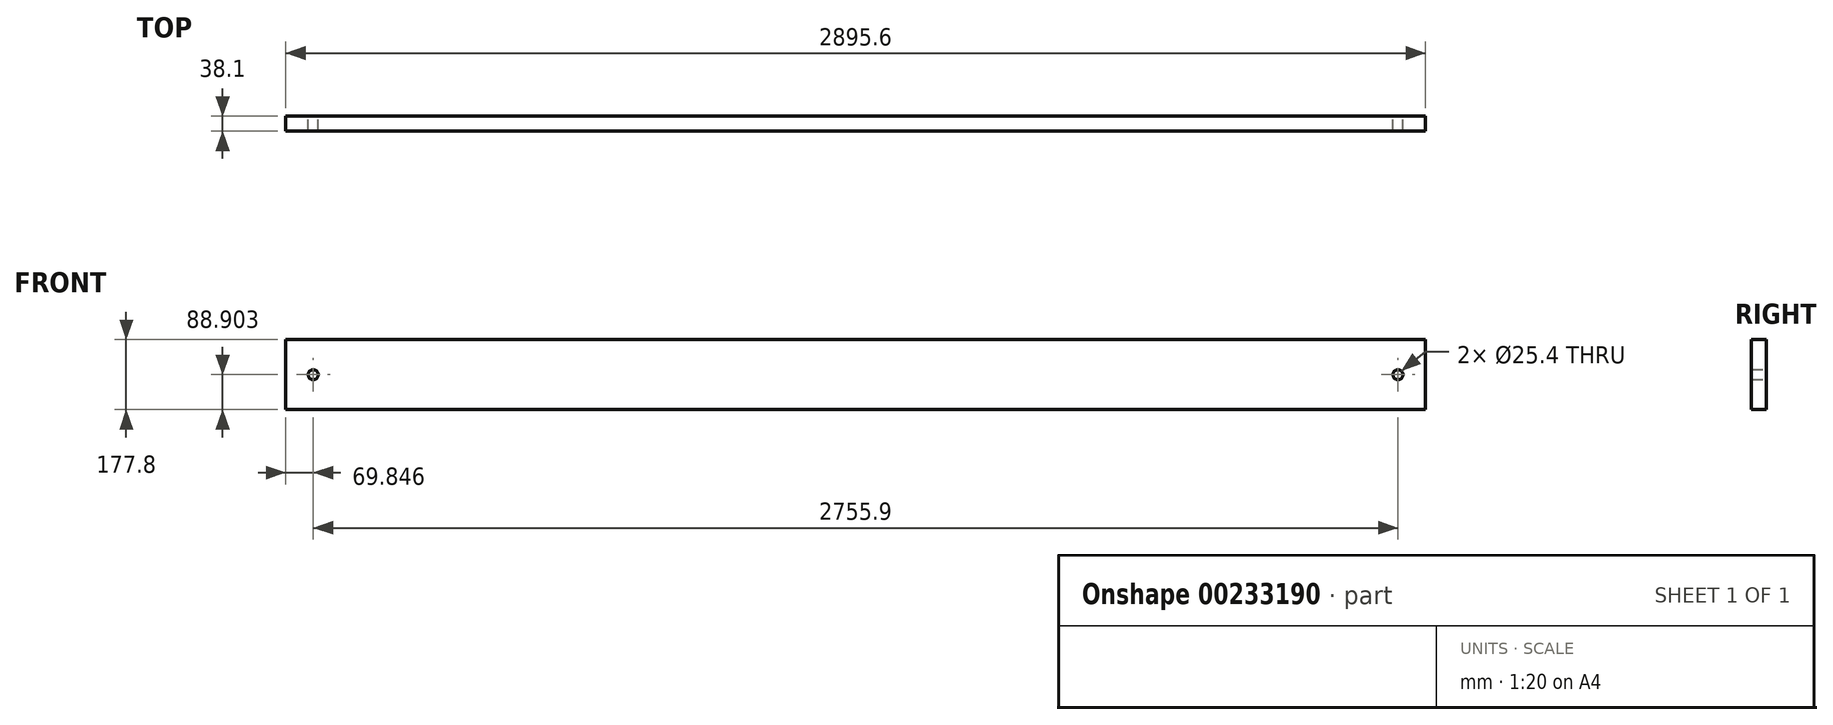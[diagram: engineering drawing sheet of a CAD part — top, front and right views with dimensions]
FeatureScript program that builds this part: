
annotation { "Feature Type Name" : "Feature", "Feature Type Description" : "" }
export const myFeature = defineFeature(function(context is Context, id is Id, definition is map)
    precondition{}
    {
        {
            var Q0;
            Q0=qCreatedBy(makeId("Front.planeOp"),FACE);
            var sketch = newSketch(context, id + "F0", { "sketchPlane" : qUnion([Q0])});
            skLineSegment(sketch, "E0.bottom", {"start": v(-1448.04, -332.84) * mm, "end": v(1447.56, -332.84) * mm});
            skLineSegment(sketch, "E0.top", {"start": v(-1448.04, -510.64) * mm, "end": v(1447.56, -510.64) * mm});
            skLineSegment(sketch, "E0.left", {"start": v(-1448.04, -332.84) * mm, "end": v(-1448.04, -510.64) * mm});
            skLineSegment(sketch, "E0.right", {"start": v(1447.56, -332.84) * mm, "end": v(1447.56, -510.64) * mm});
            skCircle(sketch, "E1", {"center": v(-1378.2, -421.74) * mm, "radius": 12.7 * mm});
            skCircle(sketch, "E2", {"center": v(1377.7, -421.74) * mm, "radius": 12.7 * mm});
            skSolve(sketch);
        }
        {
            var Q0;
            Q0 = qSketchRegion(id + "F0", true);
            extrude(context, id + "F1", {"entities" : qUnion([Q0]), "depth" : 38.1 * mm});
        }
    });
